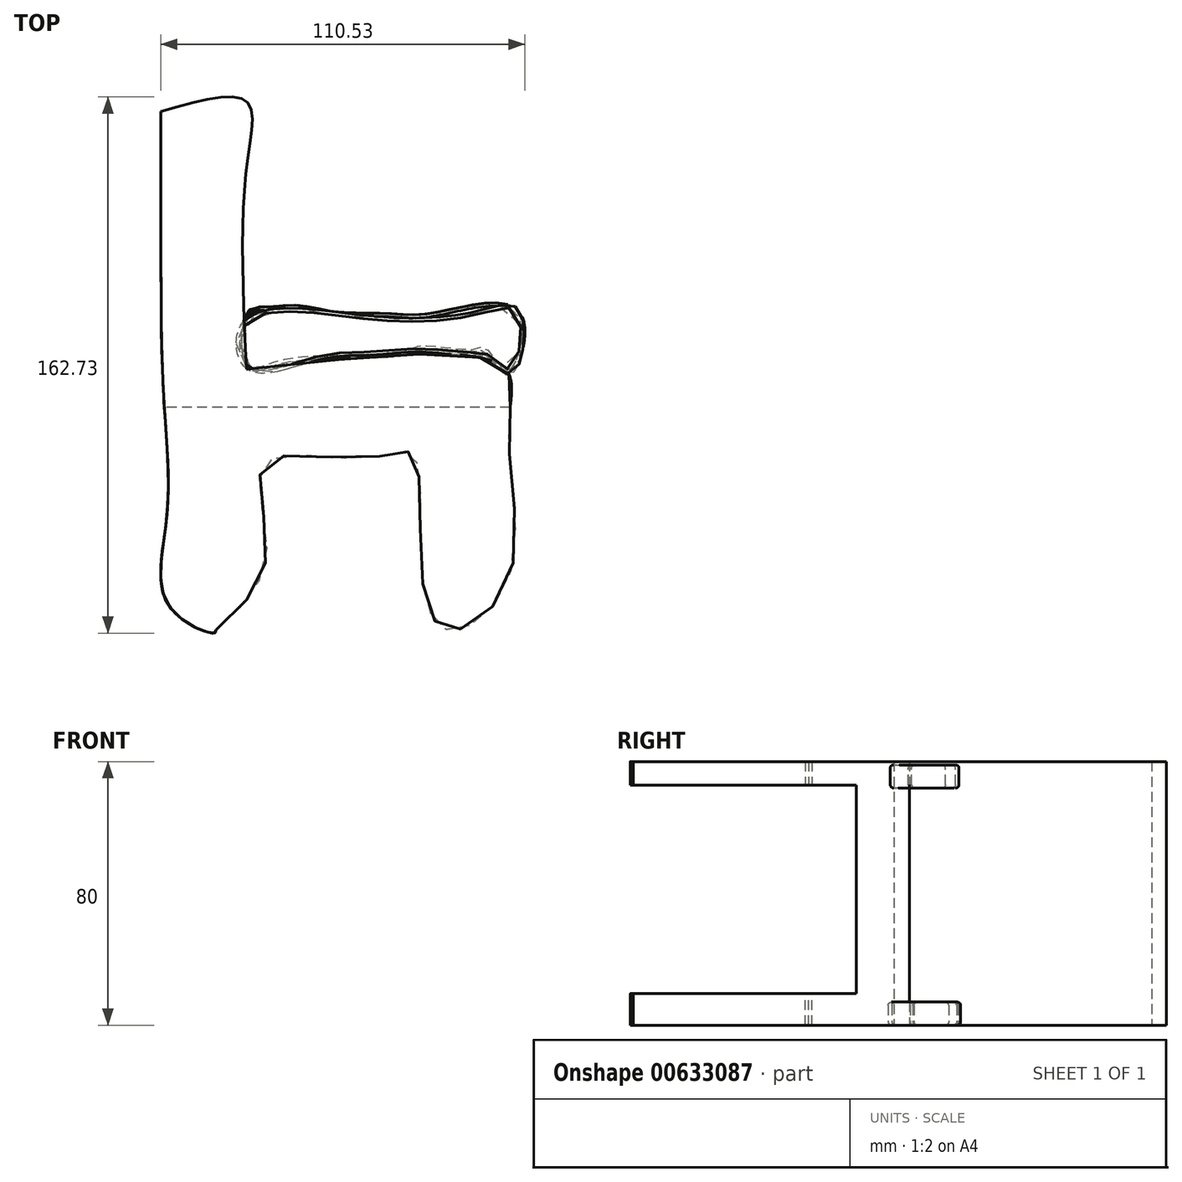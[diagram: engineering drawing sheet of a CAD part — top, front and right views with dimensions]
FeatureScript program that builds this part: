
annotation { "Feature Type Name" : "Feature", "Feature Type Description" : "" }
export const myFeature = defineFeature(function(context is Context, id is Id, definition is map)
    precondition{}
    {
        {
            var Q0;
            Q0=qCreatedBy(makeId("Top.planeOp"),FACE);
            var sketch = newSketch(context, id + "F0", { "sketchPlane" : qUnion([Q0])});
            skFitSpline(sketch, "E0", {"points": [v(-56.04, 49.44) * mm, v(-55.16, 9) * mm, v(-54.28, -26.59) * mm, v(-53.4, -53.84) * mm, v(-39.77, -61.75) * mm, v(-39.34, -60.87) * mm], "startDerivative": vector(0.6, -145.38) * mm, "endDerivative": vector(0.69, 25.33) * mm});
            skFitSpline(sketch, "E1", {"points": [v(-39.34, -60.87) * mm, v(-23.95, -38.02) * mm, v(-24.4, -10.33) * mm, v(7.25, -8.57) * mm, v(20.44, -7.7) * mm, v(23.07, -43.73) * mm, v(31.42, -60.87) * mm, v(49.44, -45.49) * mm, v(49.44, 0) * mm, v(48.13, 18.68) * mm, v(-30.1, 18.24) * mm], "startDerivative": vector(228.87, 205.22) * mm, "endDerivative": vector(-653.12, -73.82) * mm});
            skFitSpline(sketch, "E2", {"points": [v(-30.1, 18.24) * mm, v(-30.1, 78.89) * mm, v(-30.1, 99.55) * mm, v(-56.04, 96.47) * mm], "startDerivative": vector(-6.88, 147.54) * mm, "endDerivative": vector(-113, -32.45) * mm});
            skFitSpline(sketch, "E3", {"points": [v(-56.04, 96.47) * mm, v(-56.04, 49.44) * mm], "startDerivative": vector(0, -47.03) * mm, "endDerivative": vector(0, -47.03) * mm});
            skSolve(sketch);
        }
        {
            var Q0;
            Q0 = qSketchRegion(id + "F0", true);
            extrude(context, id + "F1", {"entities" : qUnion([Q0]), "depth" : 80 * mm, "offsetDistance" : 25.4 * mm});
        }
        {
            var Q0;
            Q0=qCreatedBy(makeId("Right.planeOp"),FACE);
            var sketch = newSketch(context, id + "F2", { "sketchPlane" : qUnion([Q0])});
            skLineSegment(sketch, "E4.bottom", {"start": v(-67.74, 72.86) * mm, "end": v(6.75, 72.86) * mm});
            skLineSegment(sketch, "E4.top", {"start": v(-67.74, 9.54) * mm, "end": v(6.75, 9.54) * mm});
            skLineSegment(sketch, "E4.left", {"start": v(-67.74, 72.86) * mm, "end": v(-67.74, 9.54) * mm});
            skLineSegment(sketch, "E4.right", {"start": v(6.75, 72.86) * mm, "end": v(6.75, 9.54) * mm});
            skSolve(sketch);
        }
        {
            var Q0;
            Q0 = qSketchRegion(id + "F2", true);
            extrude(context, id + "F3", {"entities" : qUnion([Q0]), "operationType" : NewBodyOperationType.REMOVE, "endBound" : BoundingType.THROUGH_ALL, "depth" : 25.4 * mm, "offsetDistance" : 25.4 * mm, "hasSecondDirection" : true, "secondDirectionOppositeDirection" : true, "secondDirectionDepth" : 60 * mm});
        }
        {
            var Q0;
            Q0=makeQuery(id+"F1.opExtrude","CAP_FACE",FACE,{"disambiguationData":[OSD([sQuery(id+"F0.wireOp",EDGE,"E0"),sQuery(id+"F0.wireOp",EDGE,"E1"),sQuery(id+"F0.wireOp",EDGE,"E2"),sQuery(id+"F0.wireOp",EDGE,"E3")])],"isStart":false});
            cPlane(context, id + "F4", {"entities" : qUnion([Q0]), "cplaneType" : CPlaneType.OFFSET, "offset" : 1 * mm, "oppositeDirection" : true, "width" : 152.4 * mm, "height" : 152.4 * mm});
        }
        {
            var Q0;
            Q0=qCreatedBy(id+"F4.planeOp",FACE);
            var sketch = newSketch(context, id + "F5", { "sketchPlane" : qUnion([Q0])});
            skFitSpline(sketch, "E5", {"points": [v(-29.77, 18.26) * mm, v(-30.73, 33.14) * mm, v(6.24, 34.58) * mm, v(40.34, 36.02) * mm, v(52.82, 36.02) * mm, v(50.9, 17.3) * mm, v(43.22, 21.62) * mm, v(35.53, 22.58) * mm, v(23.05, 23.54) * mm, v(7.68, 22.58) * mm, v(-8.16, 21.14) * mm, v(-29.77, 18.26) * mm]});
            skSolve(sketch);
        }
        {
            var Q0;
            Q0 = qSketchRegion(id + "F5", true);
            extrude(context, id + "F6", {"entities" : qUnion([Q0]), "oppositeDirection" : true, "depth" : 7 * mm, "offsetDistance" : 25.4 * mm});
        }
        {
            var Q0;
            Q0=qCreatedBy(makeId("Top.planeOp"),FACE);
            var sketch = newSketch(context, id + "F7", { "sketchPlane" : qUnion([Q0])});
            skFitSpline(sketch, "E6", {"points": [v(-29.53, 18.49) * mm, v(-30.01, 35.3) * mm, v(-23.77, 37.21) * mm, v(-14.65, 37.7) * mm, v(-3.6, 35.77) * mm, v(11.28, 35.3) * mm, v(21.37, 34.81) * mm, v(30.97, 36.25) * mm, v(48.26, 38.17) * mm, v(54.02, 32.9) * mm, v(52.58, 20.4) * mm, v(48.74, 16.57) * mm, v(42.02, 23.77) * mm, v(39.62, 23.29) * mm, v(22.33, 24.25) * mm, v(18.97, 22.8) * mm, v(-6.48, 21.37) * mm, v(-22.8, 18.97) * mm, v(-29.53, 18.49) * mm]});
            skSolve(sketch);
        }
        {
            var Q0;
            Q0 = qSketchRegion(id + "F7", true);
            extrude(context, id + "F8", {"entities" : qUnion([Q0]), "depth" : 7 * mm, "offsetDistance" : 25.4 * mm});
        }
        {
            var Q0;
            Q0=makeQuery(id+"F1.opExtrude","CAP_EDGE",EDGE,{"disambiguationData":[OSD([sQuery(id+"F0.wireOp",EDGE,"E2")])],"isStart":false});
            var Q1;
            Q1=makeQuery(id+"F1.opExtrude","CAP_EDGE",EDGE,{"disambiguationData":[OSD([sQuery(id+"F0.wireOp",EDGE,"E3")])],"isStart":false});
            var Q2;
            Q2=makeQuery(id+"F1.opExtrude","CAP_EDGE",EDGE,{"disambiguationData":[OSD([sQuery(id+"F0.wireOp",EDGE,"E1")])],"isStart":false});
            var Q3;
            Q3=makeQuery(id+"F6.opExtrude","CAP_EDGE",EDGE,{"disambiguationData":[OSD([sQuery(id+"F5.wireOp",EDGE,"E5")])],"isStart":true});
            var Q4;
            Q4=makeQuery(id+"F6.opExtrude","CAP_EDGE",EDGE,{"disambiguationData":[OSD([sQuery(id+"F5.wireOp",EDGE,"E5")])],"isStart":false});
            var Q5;
            Q5=makeQuery(id+"F8.opExtrude","CAP_EDGE",EDGE,{"disambiguationData":[OSD([sQuery(id+"F7.wireOp",EDGE,"E6")])],"isStart":true});
            var Q6;
            Q6=makeQuery(id+"F1.opExtrude","CAP_EDGE",EDGE,{"disambiguationData":[OSD([sQuery(id+"F0.wireOp",EDGE,"E1")])],"isStart":true});
            var Q7;
            Q7=makeQuery(id+"F1.opExtrude","CAP_EDGE",EDGE,{"disambiguationData":[OSD([sQuery(id+"F0.wireOp",EDGE,"E2")])],"isStart":true});
            var Q8;
            Q8=makeQuery(id+"F1.opExtrude","CAP_EDGE",EDGE,{"disambiguationData":[OSD([sQuery(id+"F0.wireOp",EDGE,"E3")])],"isStart":true});
            var Q9;
            Q9=makeQuery(id+"F1.opExtrude","CAP_FACE",FACE,{"disambiguationData":[OSD([sQuery(id+"F0.wireOp",EDGE,"E0"),sQuery(id+"F0.wireOp",EDGE,"E1"),sQuery(id+"F0.wireOp",EDGE,"E2"),sQuery(id+"F0.wireOp",EDGE,"E3")])],"isStart":true});
            var Q10;
            Q10=makeQuery(id+"F3.boolean.opBoolean","INTERSECT",EDGE,{"derivedFrom":[makeQuery(id+"F1.opExtrude","SWEPT_FACE",FACE,{"disambiguationData":[OSD([sQuery(id+"F0.wireOp",EDGE,"E1")])]}),makeQuery(id+"F3.opExtrude","SWEPT_FACE",FACE,{"disambiguationData":[OSD([sQuery(id+"F2.wireOp",EDGE,"E4.right")])]})]});
            var Q11;
            Q11=makeQuery(id+"F3.boolean.opBoolean","INTERSECT",EDGE,{"derivedFrom":[makeQuery(id+"F1.opExtrude","SWEPT_FACE",FACE,{"disambiguationData":[OSD([sQuery(id+"F0.wireOp",EDGE,"E1")])]}),makeQuery(id+"F3.opExtrude","SWEPT_FACE",FACE,{"disambiguationData":[OSD([sQuery(id+"F2.wireOp",EDGE,"E4.top")])]})]});
            var Q12;
            Q12=makeQuery(id+"F3.boolean.opBoolean","INTERSECT",EDGE,{"derivedFrom":[makeQuery(id+"F1.opExtrude","SWEPT_FACE",FACE,{"disambiguationData":[OSD([sQuery(id+"F0.wireOp",EDGE,"E0")])]}),makeQuery(id+"F3.opExtrude","SWEPT_FACE",FACE,{"disambiguationData":[OSD([sQuery(id+"F2.wireOp",EDGE,"E4.top")])]})]});
            var Q13;
            Q13=makeQuery(id+"F3.boolean.opBoolean","INTERSECT",EDGE,{"derivedFrom":[makeQuery(id+"F1.opExtrude","SWEPT_FACE",FACE,{"disambiguationData":[OSD([sQuery(id+"F0.wireOp",EDGE,"E0")])]}),makeQuery(id+"F3.opExtrude","SWEPT_FACE",FACE,{"disambiguationData":[OSD([sQuery(id+"F2.wireOp",EDGE,"E4.right")])]})]});
            var Q14;
            Q14=makeQuery(id+"F1.opExtrude","SWEPT_EDGE",EDGE,{"disambiguationData":[OSD([sQuery(id+"F0.wireOp",EDGE,"E1"),sQuery(id+"F0.wireOp",EDGE,"E2")])]});
            var Q15;
            Q15=makeQuery(id+"F3.boolean.opBoolean","INTERSECT",EDGE,{"derivedFrom":[makeQuery(id+"F1.opExtrude","SWEPT_FACE",FACE,{"disambiguationData":[OSD([sQuery(id+"F0.wireOp",EDGE,"E1")])]}),makeQuery(id+"F3.opExtrude","SWEPT_FACE",FACE,{"disambiguationData":[OSD([sQuery(id+"F2.wireOp",EDGE,"E4.bottom")])]})]});
            var Q16;
            Q16=makeQuery(id+"F3.boolean.opBoolean","COPY",FACE,{"derivedFrom":makeQuery(id+"F3.opExtrude","SWEPT_FACE",FACE,{"disambiguationData":[OSD([sQuery(id+"F2.wireOp",EDGE,"E4.top")])]})});
            var Q17;
            Q17=makeQuery(id+"F1.opExtrude","SWEPT_EDGE",EDGE,{"disambiguationData":[OSD([sQuery(id+"F0.wireOp",EDGE,"E2"),sQuery(id+"F0.wireOp",EDGE,"E3")])]});
            var Q18;
            Q18=makeQuery(id+"F1.opExtrude","SWEPT_FACE",FACE,{"disambiguationData":[OSD([sQuery(id+"F0.wireOp",EDGE,"E2")])]});
            var Q19;
            Q19=makeQuery(id+"F6.opExtrude","SWEPT_FACE",FACE,{"disambiguationData":[OSD([sQuery(id+"F5.wireOp",EDGE,"E5")])]});
            var Q20;
            Q20=makeQuery(id+"F8.opExtrude","SWEPT_FACE",FACE,{"disambiguationData":[OSD([sQuery(id+"F7.wireOp",EDGE,"E6")])]});
            var Q21;
            Q21=makeQuery(id+"F1.opExtrude","SWEPT_FACE",FACE,{"disambiguationData":[OSD([sQuery(id+"F0.wireOp",EDGE,"E0")])]});
            fillet(context, id + "F9", {"entities" : qUnion([Q0, Q1, Q2, Q3, Q4, Q5, Q6, Q7, Q8, Q9, Q10, Q11, Q12, Q13, Q14, Q15, Q16, Q17, Q18, Q19, Q20, Q21]), "radius" : 1 * mm, "tangentPropagation" : true, "allowEdgeOverflow" : false});
        }
    });
